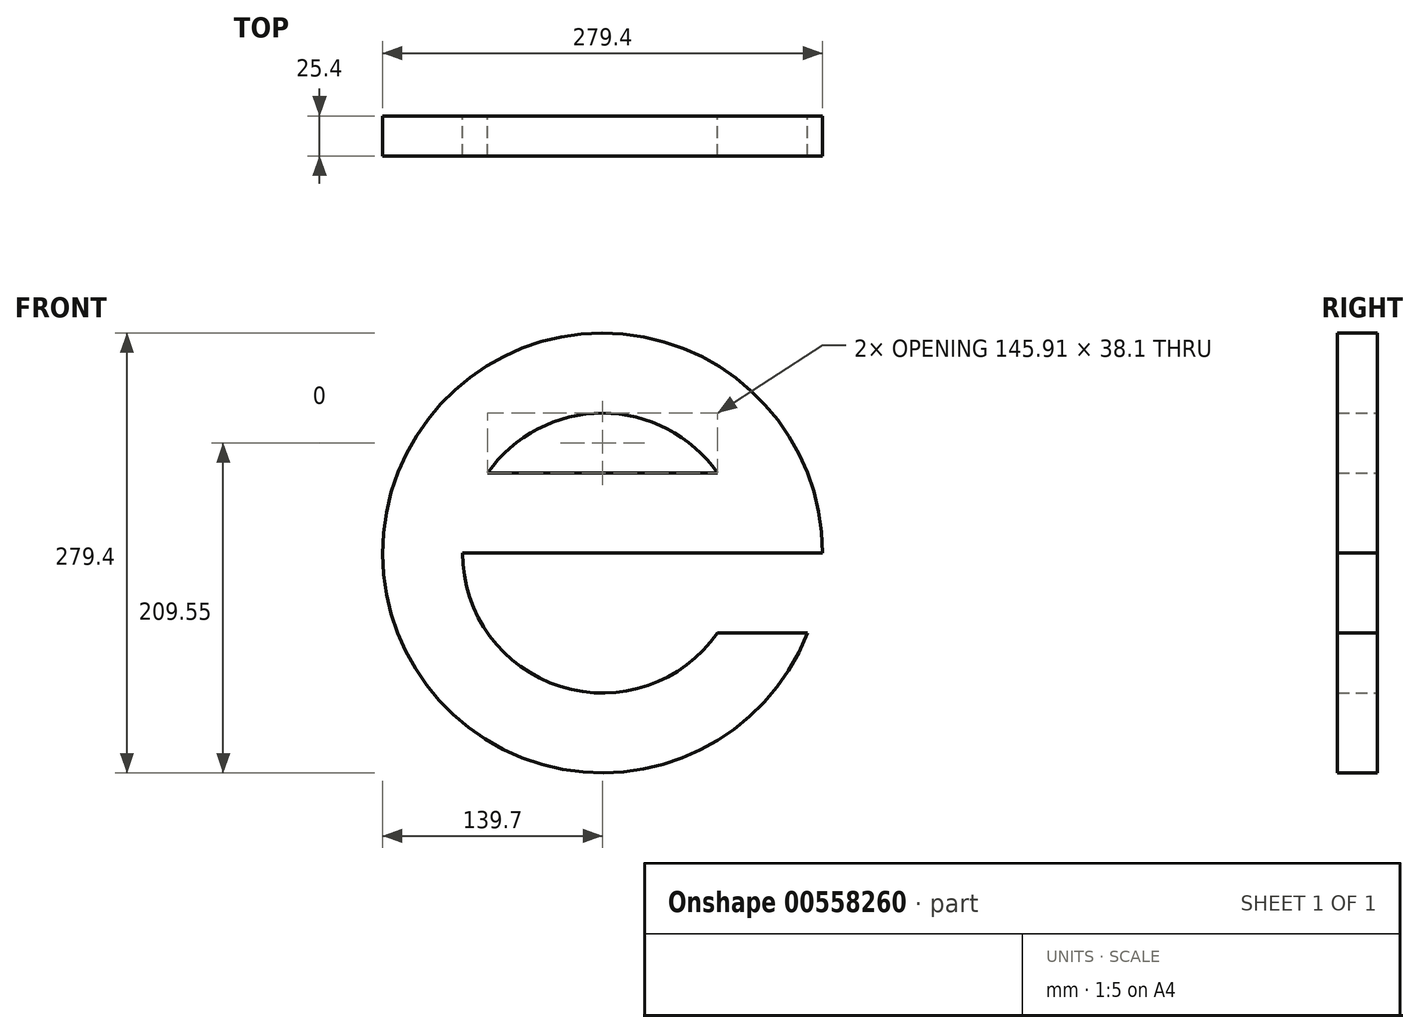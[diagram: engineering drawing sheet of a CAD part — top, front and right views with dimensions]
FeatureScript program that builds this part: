
annotation { "Feature Type Name" : "Feature", "Feature Type Description" : "" }
export const myFeature = defineFeature(function(context is Context, id is Id, definition is map)
    precondition{}
    {
        {
            var Q0;
            Q0=qCreatedBy(makeId("Front.planeOp"),FACE);
            var sketch = newSketch(context, id + "F0", { "sketchPlane" : qUnion([Q0])});
            skArc(sketch, "E0", {"start": v(139.7, 0) * mm, "mid": v(-137.29, 25.85) * mm, "end": v(130.14, -50.8) * mm});
            skArc(sketch, "E1", {"start": v(-88.9, 0) * mm, "mid": v(-26.62, -84.82) * mm, "end": v(72.96, -50.8) * mm});
            skLineSegment(sketch, "E2", {"start": v(139.7, 0) * mm, "end": v(88.9, 0) * mm});
            skLineSegment(sketch, "E3", {"start": v(88.9, 0) * mm, "end": v(-88.9, 0) * mm});
            skLineSegment(sketch, "E4", {"start": v(72.96, 50.8) * mm, "end": v(-72.96, 50.8) * mm});
            skPoint(sketch, "E5.end.orphan", {"position": v(0, 50.8) * mm});
            skArc(sketch, "E6.trimOffspring", {"start": v(72.96, 50.8) * mm, "mid": v(0, 88.9) * mm, "end": v(-72.96, 50.8) * mm});
            skLineSegment(sketch, "E7", {"start": v(130.14, -50.8) * mm, "end": v(72.96, -50.8) * mm});
            skSolve(sketch);
        }
        {
            var Q0;
            Q0 = qSketchRegion(id + "F0", true);
            extrude(context, id + "F1", {"entities" : qUnion([Q0]), "depth" : 25.4 * mm, "offsetDistance" : 25.4 * mm});
        }
    });
